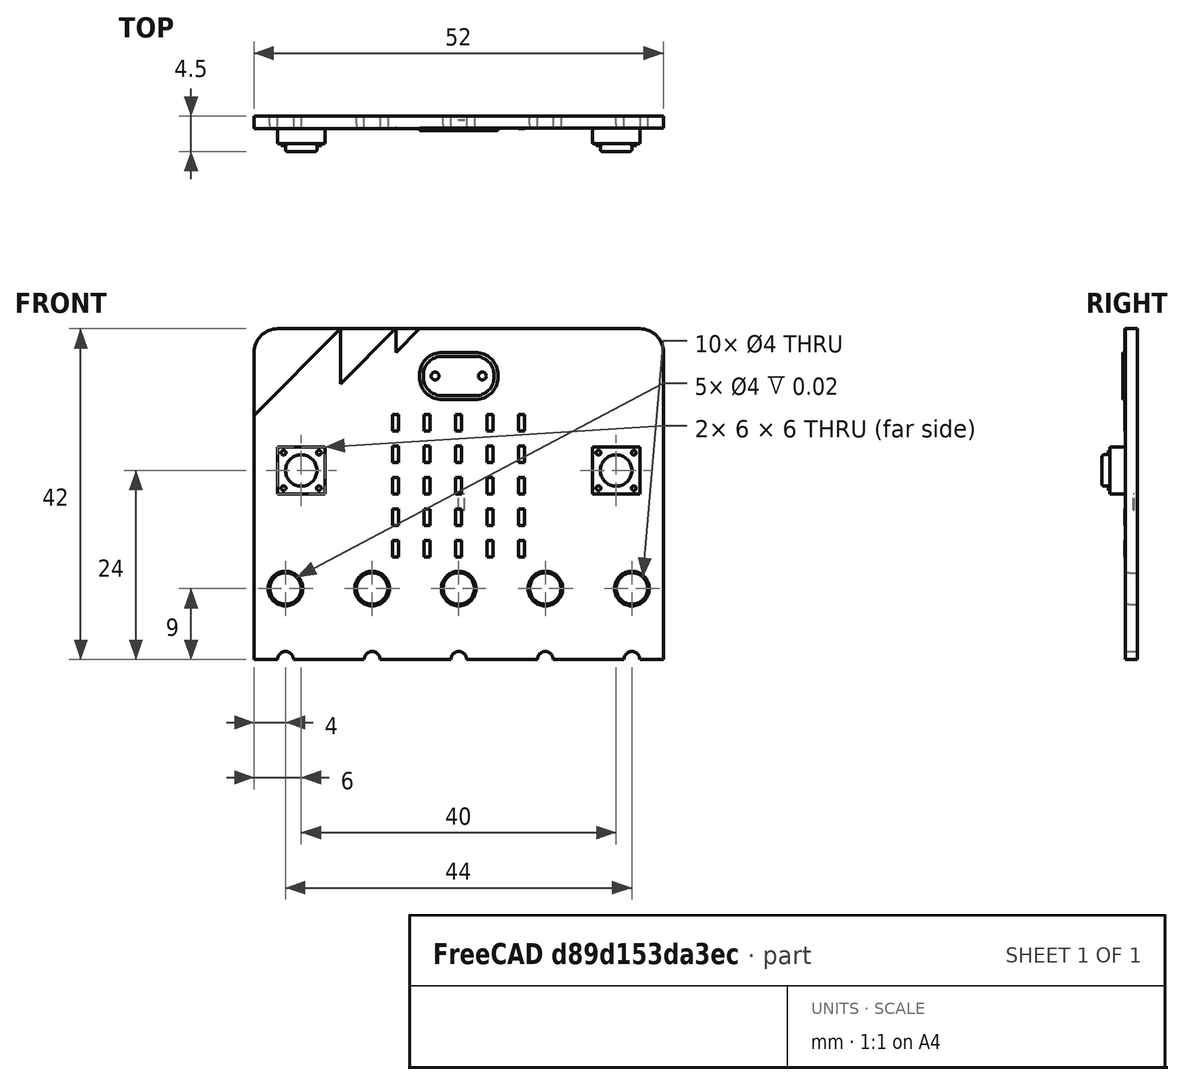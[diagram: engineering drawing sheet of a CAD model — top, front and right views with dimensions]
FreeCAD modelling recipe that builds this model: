
FCSTD DOCUMENT  (FreeCAD 0.20R29603 (Git))
Label: Placa_Microbit
License: All rights reserved
LicenseURL: http://en.wikipedia.org/wiki/All_rights_reserved
objects: Part::Cylinder×22, Part::MultiFuse×22, Part::Cut×16, Part::Box×15, Part::Fillet×8, Part::FeaturePython×6
note: 88 computed .brp shape members not serialized (recipe doc carries the construction recipe); baked Part::Feature solids carry a one-line shape summary decoded from their .brp

FEATURE [Part::Box] Box004  label="Cubo"
  AttacherType = Attacher::AttachEngine3D
  Height = 34
  Length = 52
  Placement = pos=(-26,-25,69) rot=(0,0,1;0rad)
  Width = 1.5
FEATURE [Part::Box] Box186  label="Cubo174"
  AttacherType = Attacher::AttachEngine3D
  Height = 8
  Length = 52
  Placement = pos=(-26,-25,61) rot=(0,0,1;0rad)
  Width = 1.5
FEATURE [Part::Box] Box187  label="Cubo175"
  AttacherType = Attacher::AttachEngine3D
  Height = 11
  Length = 11
  Placement = pos=(-56,-25,61) rot=(0,0,1;0rad)
  Width = 0.2
FEATURE [Part::Box] Box188  label="Cubo176"
  AttacherType = Attacher::AttachEngine3D
  Height = 8
  Length = 52
  Placement = pos=(-61,-25,44.685) rot=(0,-1,0;0.785398rad)
  Width = 1.5
FEATURE [Part::Box] Box189  label="Cubo177"
  AttacherType = Attacher::AttachEngine3D
  Height = 11
  Length = 11
  Placement = pos=(-56,-25,61) rot=(0,0,1;0rad)
  Width = 0.2
FEATURE [Part::Box] Box190  label="Cubo178"
  AttacherType = Attacher::AttachEngine3D
  Height = 8
  Length = 52
  Placement = pos=(-61,-25,44.685) rot=(0,-1,0;0.785398rad)
  Width = 1.5
FEATURE [Part::Box] Box191  label="Cubo179"
  AttacherType = Attacher::AttachEngine3D
  Height = 11
  Length = 11
  Placement = pos=(-56,-25,61) rot=(0,0,1;0rad)
  Width = 0.2
FEATURE [Part::Box] Box192  label="Cubo180"
  AttacherType = Attacher::AttachEngine3D
  Height = 8
  Length = 52
  Placement = pos=(-61,-25,44.685) rot=(0,-1,0;0.785398rad)
  Width = 1.5
FEATURE [Part::Box] Box193  label="Cubo181"
  AttacherType = Attacher::AttachEngine3D
  Height = 8
  Length = 52
  Placement = pos=(-26,-26,103) rot=(0,0,1;0rad)
  Width = 1.5
FEATURE [Part::Box] Box194  label="Cubo182"
  AttacherType = Attacher::AttachEngine3D
  Height = 8
  Length = 52
  Placement = pos=(-26,-26,103) rot=(0,0,1;0rad)
  Width = 1.5
FEATURE [Part::Box] Box195  label="Led"
  AttacherType = Attacher::AttachEngine3D
  Height = 2.1
  Length = 0.75
  Width = 0.1
FEATURE [Part::FeaturePython] Array  # Draft array (typed FeaturePython)
  AlwaysSyncPlacement = false
  Angle = 360
  ArrayType = 0
  Axis = (0,0,1)
  Base = -> Box195
  Center = (0,0,0)
  Count = 25
  ExpandArray = false
  Fuse = false
  IntervalAxis = (0,0,0)
  IntervalX = (4,0,0)
  IntervalY = (0,100,0)
  IntervalZ = (0,0,4)
  NumberCircles = 3
  NumberPolar = 5
  NumberX = 5
  NumberY = 1
  NumberZ = 5
  Placement = pos=(-8.4,-25.1,74) rot=(0,0,1;0rad)
  PlacementList = 25 placements: [(0,0,0),(0,0,4),(0,0,8),(0,0,12),(0,0,16),(4,0,0),(4,0,4),(4,0,8),(4,0,12),(4,0,16),(8,0,0),(8,0,4),(8,0,8),(8,0,12),(8,0,16),(12,0,0),(12,0,4),(12,0,8),(12,0,12),(12,0,16),(16,0,0),(16,0,4),(16,0,8),(16,0,12),(16,0,16)]
  RadialDistance = 50
  ScaleList = (25) [(1,1,1),(1,1,1),(1,1,1),(1,1,1),(1,1,1),(1,1,1),(1,1,1),(1,1,1),(1,1,1),(1,1,1),(1,1,1),(1,1,1),(1,1,1),(1,1,1),(1,1,1),(1,1,1),(1,1,1),(1,1,1),+7 more]
  Symmetry = 1
  TangentialDistance = 25
FEATURE [Part::Box] Box196  label="Cubo183"
  AttacherType = Attacher::AttachEngine3D
  Height = 6
  Length = 6
  Width = 3.5
FEATURE [Part::Box] Box199  label="Cubo186"
  AttacherType = Attacher::AttachEngine3D
  Height = 6
  Length = 6
  Width = 3.5
FEATURE [Part::Box] Box200  label="Cubo187"
  AttacherType = Attacher::AttachEngine3D
  Height = 6
  Length = 10
  Width = 1
FEATURE [Part::Box] Box201  label="Cubo188"
  AttacherType = Attacher::AttachEngine3D
  Height = 5
  Length = 9
  Placement = pos=(0.5,0,0.5) rot=(0,0,1;0rad)
  Width = 1
FEATURE [Part::Cut] Cut240
  Base = -> Box187
  Tool = -> Box188
FEATURE [Part::Cut] Cut241
  Base = -> Box189
  Placement = pos=(41,-0.1,35) rot=(0,0,1;0rad)
  Tool = -> Box190
FEATURE [Part::Cut] Cut242
  Base = -> Box191
  Placement = pos=(48.05,-0.1,39) rot=(0,0,1;0rad)
  Tool = -> Box192
FEATURE [Part::Cut] Cut243
  Base = -> Cut242
  Tool = -> Box193
FEATURE [Part::Cut] Cut244
  Base = -> Cut241
  Tool = -> Box194
FEATURE [Part::Cylinder] Cylinder167  label="Cilindro167"
  Angle = 360
  AttacherType = Attacher::AttachEngine3D
  FirstAngle = 0
  Height = 10
  Placement = pos=(0,-15,70) rot=(1,0,0;1.5708rad)
  Radius = 2
  SecondAngle = 0
FEATURE [Part::Cylinder] Cylinder168  label="Cilindro168"
  Angle = 360
  AttacherType = Attacher::AttachEngine3D
  FirstAngle = 0
  Height = 10
  Placement = pos=(-11,-15,70) rot=(1,0,0;1.5708rad)
  Radius = 2
  SecondAngle = 0
FEATURE [Part::Cylinder] Cylinder169  label="Cilindro169"
  Angle = 360
  AttacherType = Attacher::AttachEngine3D
  FirstAngle = 0
  Height = 10
  Placement = pos=(-22,-15,70) rot=(1,0,0;1.5708rad)
  Radius = 2
  SecondAngle = 0
FEATURE [Part::Cylinder] Cylinder170  label="Cilindro170"
  Angle = 360
  AttacherType = Attacher::AttachEngine3D
  FirstAngle = 0
  Height = 10
  Placement = pos=(11,-15,70) rot=(1,0,0;1.5708rad)
  Radius = 2
  SecondAngle = 0
FEATURE [Part::Cylinder] Cylinder171  label="Cilindro171"
  Angle = 360
  AttacherType = Attacher::AttachEngine3D
  FirstAngle = 0
  Height = 10
  Placement = pos=(22,-15,70) rot=(1,0,0;1.5708rad)
  Radius = 2
  SecondAngle = 0
FEATURE [Part::Cylinder] Cylinder172  label="Cilindro172"
  Angle = 360
  AttacherType = Attacher::AttachEngine3D
  FirstAngle = 0
  Height = 10
  Placement = pos=(0,-16,61) rot=(1,0,0;1.5708rad)
  Radius = 1
  SecondAngle = 0
FEATURE [Part::Cylinder] Cylinder173  label="Cilindro173"
  Angle = 360
  AttacherType = Attacher::AttachEngine3D
  FirstAngle = 0
  Height = 10
  Placement = pos=(-11,-16,61) rot=(1,0,0;1.5708rad)
  Radius = 1
  SecondAngle = 0
FEATURE [Part::Cylinder] Cylinder174  label="Cilindro174"
  Angle = 360
  AttacherType = Attacher::AttachEngine3D
  FirstAngle = 0
  Height = 10
  Placement = pos=(-22,-16,61) rot=(1,0,0;1.5708rad)
  Radius = 1
  SecondAngle = 0
FEATURE [Part::Cylinder] Cylinder175  label="Cilindro175"
  Angle = 360
  AttacherType = Attacher::AttachEngine3D
  FirstAngle = 0
  Height = 10
  Placement = pos=(11,-16,61) rot=(1,0,0;1.5708rad)
  Radius = 1
  SecondAngle = 0
FEATURE [Part::Cylinder] Cylinder176  label="Cilindro176"
  Angle = 360
  AttacherType = Attacher::AttachEngine3D
  FirstAngle = 0
  Height = 10
  Placement = pos=(22,-16,61) rot=(1,0,0;1.5708rad)
  Radius = 1
  SecondAngle = 0
FEATURE [Part::Cylinder] Cylinder177  label="Cilindro177"
  Angle = 360
  AttacherType = Attacher::AttachEngine3D
  FirstAngle = 0
  Height = 1
  Placement = pos=(3,0,3) rot=(1,0,0;1.5708rad)
  Radius = 2
  SecondAngle = 0
FEATURE [Part::Cylinder] Cylinder178  label="Cilindro178"
  Angle = 360
  AttacherType = Attacher::AttachEngine3D
  FirstAngle = 0
  Height = 0.2
  Placement = pos=(0.75,0,0.75) rot=(1,0,0;1.5708rad)
  Radius = 0.3
  SecondAngle = 0
FEATURE [Part::Cylinder] Cylinder179  label="Cilindro179"
  Angle = 360
  AttacherType = Attacher::AttachEngine3D
  FirstAngle = 0
  Height = 0.2
  Placement = pos=(0.75,0,5.25) rot=(1,0,0;1.5708rad)
  Radius = 0.3
  SecondAngle = 0
FEATURE [Part::Cylinder] Cylinder180  label="Cilindro180"
  Angle = 360
  AttacherType = Attacher::AttachEngine3D
  FirstAngle = 0
  Height = 0.2
  Placement = pos=(5.25,0,0.75) rot=(1,0,0;1.5708rad)
  Radius = 0.3
  SecondAngle = 0
FEATURE [Part::Cylinder] Cylinder181  label="Cilindro181"
  Angle = 360
  AttacherType = Attacher::AttachEngine3D
  FirstAngle = 0
  Height = 0.2
  Placement = pos=(5.25,0,5.25) rot=(1,0,0;1.5708rad)
  Radius = 0.3
  SecondAngle = 0
FEATURE [Part::Cylinder] Cylinder182  label="Cilindro182"
  Angle = 360
  AttacherType = Attacher::AttachEngine3D
  FirstAngle = 0
  Height = 1
  Placement = pos=(3,0,3) rot=(1,0,0;1.5708rad)
  Radius = 2
  SecondAngle = 0
FEATURE [Part::Cylinder] Cylinder183  label="Cilindro183"
  Angle = 360
  AttacherType = Attacher::AttachEngine3D
  FirstAngle = 0
  Height = 0.2
  Placement = pos=(0.75,0,0.75) rot=(1,0,0;1.5708rad)
  Radius = 0.3
  SecondAngle = 0
FEATURE [Part::Cylinder] Cylinder184  label="Cilindro184"
  Angle = 360
  AttacherType = Attacher::AttachEngine3D
  FirstAngle = 0
  Height = 0.2
  Placement = pos=(0.75,0,5.25) rot=(1,0,0;1.5708rad)
  Radius = 0.3
  SecondAngle = 0
FEATURE [Part::Cylinder] Cylinder185  label="Cilindro185"
  Angle = 360
  AttacherType = Attacher::AttachEngine3D
  FirstAngle = 0
  Height = 0.2
  Placement = pos=(5.25,0,0.75) rot=(1,0,0;1.5708rad)
  Radius = 0.3
  SecondAngle = 0
FEATURE [Part::Cylinder] Cylinder186  label="Cilindro186"
  Angle = 360
  AttacherType = Attacher::AttachEngine3D
  FirstAngle = 0
  Height = 0.2
  Placement = pos=(5.25,0,5.25) rot=(1,0,0;1.5708rad)
  Radius = 0.3
  SecondAngle = 0
FEATURE [Part::Cylinder] Cylinder187  label="Cilindro187"
  Angle = 360
  AttacherType = Attacher::AttachEngine3D
  FirstAngle = 0
  Height = 1
  Placement = pos=(-3,-24.3,97) rot=(1,0,0;1.5708rad)
  Radius = 0.5
  SecondAngle = 0
FEATURE [Part::Cylinder] Cylinder188  label="Cilindro188"
  Angle = 360
  AttacherType = Attacher::AttachEngine3D
  FirstAngle = 0
  Height = 1
  Placement = pos=(3,-24.3,97) rot=(1,0,0;1.5708rad)
  Radius = 0.5
  SecondAngle = 0
FEATURE [Part::Fillet] Fillet014  label="Microbit"
  Base = -> Box004
  Edges = 2 edges r=3: [Edge2,Edge6]
FEATURE [Part::Fillet] Fillet153
  Base = -> Cut240
  Edges = 1 edges r=3: [Edge2]
  Placement = pos=(30,-0.1,31) rot=(0,0,1;0rad)
FEATURE [Part::Fillet] Fillet154
  Base = -> Cylinder177
  Edges = 1 edges r=0.3: [Edge3]
FEATURE [Part::Fillet] Fillet155
  Base = -> Cylinder182
  Edges = 1 edges r=0.3: [Edge3]
FEATURE [Part::Fillet] Fillet156
  Base = -> Box200
  Edges = 2 edges r=2.9: [Edge6,Edge8]
FEATURE [Part::Fillet] Fillet157
  Base = -> Fillet156
  Edges = 2 edges r=2.9: [Edge17,Edge18]
FEATURE [Part::Fillet] Fillet158
  Base = -> Box201
  Edges = 2 edges r=2.4: [Edge6,Edge8]
FEATURE [Part::Fillet] Fillet159
  Base = -> Fillet158
  Edges = 2 edges r=2.4: [Edge17,Edge18]
FEATURE [Part::Cut] Cut257
  Base = -> Fillet157
  Placement = pos=(-5,-25.3,94) rot=(0,0,1;0rad)
  Tool = -> Fillet159
FEATURE [Part::MultiFuse] Fusion114
  Shapes = -> [Fillet014,Fillet153]
FEATURE [Part::MultiFuse] Fusion115
  Shapes = -> [Fusion114,Cut243]
FEATURE [Part::MultiFuse] Fusion116  label="Microbit001"
  Shapes = -> [Fusion115,Cut244]
FEATURE [Part::MultiFuse] Fusion117
  Shapes = -> [Box186,Fusion116]
FEATURE [Part::MultiFuse] Fusion118
  Shapes = -> [Array,Fusion117]
FEATURE [Part::Cut] Cut245
  Base = -> Fusion118
  Tool = -> Cylinder167
FEATURE [Part::Cut] Cut246
  Base = -> Cut245
  Tool = -> Cylinder171
FEATURE [Part::Cut] Cut247
  Base = -> Cut246
  Tool = -> Cylinder170
FEATURE [Part::Cut] Cut248
  Base = -> Cut247
  Tool = -> Cylinder169
FEATURE [Part::Cut] Cut249
  Base = -> Cut248
  Tool = -> Cylinder168
FEATURE [Part::Cut] Cut250
  Base = -> Cut249
  Tool = -> Cylinder172
FEATURE [Part::Cut] Cut251
  Base = -> Cut250
  Tool = -> Cylinder176
FEATURE [Part::Cut] Cut252
  Base = -> Cut251
  Tool = -> Cylinder175
FEATURE [Part::Cut] Cut253
  Base = -> Cut252
  Tool = -> Cylinder174
FEATURE [Part::Cut] Cut254
  Base = -> Cut253
  Tool = -> Cylinder173
FEATURE [Part::MultiFuse] Fusion119
  Shapes = -> [Box196,Cylinder178]
FEATURE [Part::MultiFuse] Fusion120
  Shapes = -> [Fusion119,Cylinder181]
FEATURE [Part::MultiFuse] Fusion121
  Shapes = -> [Fusion120,Cylinder180]
FEATURE [Part::MultiFuse] Fusion122
  Shapes = -> [Fusion121,Cylinder179]
FEATURE [Part::MultiFuse] Fusion123  label="BotonMicrobit"
  Placement = pos=(-23,-27,82) rot=(0,0,1;0rad)
  Shapes = -> [Fusion122,Fillet154]
FEATURE [Part::MultiFuse] Fusion124
  Shapes = -> [Box199,Cylinder183]
FEATURE [Part::MultiFuse] Fusion125
  Shapes = -> [Fusion124,Cylinder186]
FEATURE [Part::MultiFuse] Fusion126
  Shapes = -> [Fusion125,Cylinder185]
FEATURE [Part::MultiFuse] Fusion127
  Shapes = -> [Fusion126,Cylinder184]
FEATURE [Part::MultiFuse] Fusion128  label="BotonMicrobit001"
  Placement = pos=(17,-27,82) rot=(0,0,1;0rad)
  Shapes = -> [Fusion127,Fillet155]
FEATURE [Part::MultiFuse] Fusion129
  Shapes = -> [Cut254,Cylinder187]
FEATURE [Part::MultiFuse] Fusion130
  Shapes = -> [Fusion129,Cylinder188]
FEATURE [Part::MultiFuse] Fusion131
  Shapes = -> [Fusion130,Cut257]
FEATURE [Part::MultiFuse] Fusion132
  Shapes = -> [Fusion131,Fusion123]
FEATURE [Part::MultiFuse] Fusion133  label="PlacaMicrobit"
  Shapes = -> [Fusion132,Fusion128]
FEATURE [Part::FeaturePython] Tube014  # WARN: FeaturePython — macro-defined, semantics opaque (R4)
  AttacherType = Attacher::AttachEngine3D
  Height = 0.5
  InnerRadius = 2
  OuterRadius = 2.2
  Placement = pos=(0,-24.5,70) rot=(1,0,0;1.5708rad)
FEATURE [Part::FeaturePython] Tube015  # WARN: FeaturePython — macro-defined, semantics opaque (R4)
  AttacherType = Attacher::AttachEngine3D
  Height = 0.5
  InnerRadius = 2
  OuterRadius = 2.2
  Placement = pos=(11,-24.5,70) rot=(1,0,0;1.5708rad)
FEATURE [Part::FeaturePython] Tube016  # WARN: FeaturePython — macro-defined, semantics opaque (R4)
  AttacherType = Attacher::AttachEngine3D
  Height = 0.5
  InnerRadius = 2
  OuterRadius = 2.2
  Placement = pos=(22,-24.5,70) rot=(1,0,0;1.5708rad)
FEATURE [Part::FeaturePython] Tube017  # WARN: FeaturePython — macro-defined, semantics opaque (R4)
  AttacherType = Attacher::AttachEngine3D
  Height = 0.5
  InnerRadius = 2
  OuterRadius = 2.2
  Placement = pos=(-11,-24.5,70) rot=(1,0,0;1.5708rad)
FEATURE [Part::FeaturePython] Tube018  # WARN: FeaturePython — macro-defined, semantics opaque (R4)
  AttacherType = Attacher::AttachEngine3D
  Height = 0.5
  InnerRadius = 2
  OuterRadius = 2.2
  Placement = pos=(-22,-24.5,70) rot=(1,0,0;1.5708rad)
FEATURE [Part::MultiFuse] Fusion226
  Placement = pos=(0,-0.02,0) rot=(0,0,1;0rad)
  Shapes = -> [Tube014,Tube015,Tube016,Tube017,Tube018]
FEATURE [Part::MultiFuse] Fusion227  label="Placa_Microbit"
  Placement = pos=(0,24,-80) rot=(0,0,1;0rad)
  Shapes = -> [Fusion226,Fusion133]
